# Revit family: Bike-Lockers_Huntco_BV1
name_source: partatom
category: Site
units: mm (PartAtom-declared; Revit-internal decimal feet)

## family parameters
Classification Number = 23.40.10.11.11
Cut with Voids When Loaded = No
Host = Face
Part Type = Normal
Round Connector Dimension = Use Diameter
Shared = No

## types (1)
- Bike-Lockers_Huntco_BV1
    Assembly Code = G2040500
    Capacity = 1 Bike
    Construction Details = http://www.arcat.com
    Default Elevation = 4' - 0"
    Description = Huntco BV-1 Bike Locker
    Door Panel Perforations = Yes
    Expected Lifespan (Years) = 0
    Green Building-LEED = http://www.arcat.com
    Handle = Metal - Steel - Huntco - Stainless
    Keynote = 02871
    Locker Color = Metal - Steel - Huntco - Powdercoat as Specified
    Maintenance Schedule (Months) = 0
    Manufacturer = Huntco Supply LLC
    Manufacturer Fax = 503-274-2055
    Manufacturer Website = http://www.huntco.com
    Model = BV-1
    Product Data = http://www.arcat.com
    Regular Panels = No
    Revision = R1_11_2012
    Send Message = http://www.arcat.com
    Sidewall Panel Perforations = Yes
    Specification = http://www.arcat.com
    URL = http://www.huntco.com
    Unit Height = 3' - 11"
    Unit Length = 6' - 4"
    Unit Weight = 0
    Unit Width = 3' - 3"
    Warranty Duration (Years) = 0

## geometry (parser evidence)
native form markers: Blend x18, Sweep x2
no freeform markers — native parametric forms only
